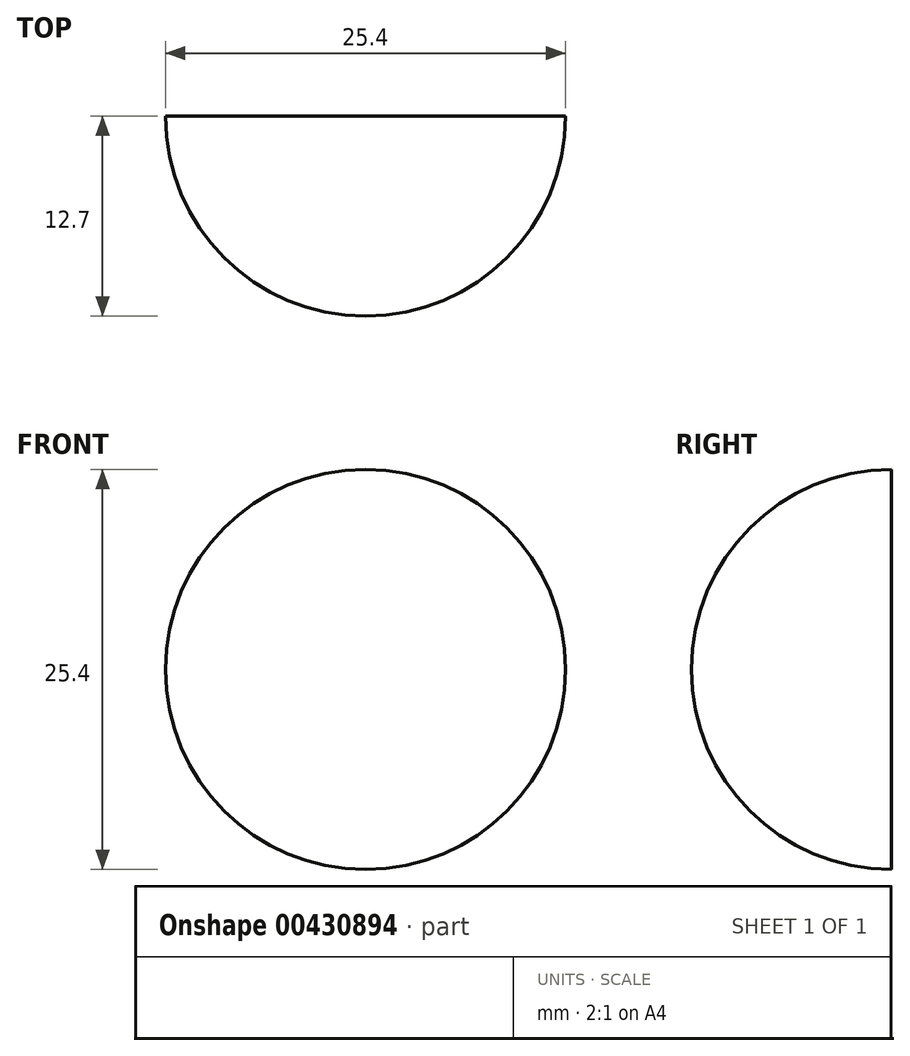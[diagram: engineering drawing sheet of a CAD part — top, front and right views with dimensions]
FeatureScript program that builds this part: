
annotation { "Feature Type Name" : "Feature", "Feature Type Description" : "" }
export const myFeature = defineFeature(function(context is Context, id is Id, definition is map)
    precondition{}
    {
        {
            var Q0;
            Q0=qCreatedBy(makeId("Front.planeOp"),FACE);
            var sketch = newSketch(context, id + "F0", { "sketchPlane" : qUnion([Q0])});
            skArc(sketch, "E0", {"start": v(0, 12.7) * mm, "mid": v(-12.7, 0) * mm, "end": v(0, -12.7) * mm});
            skLineSegment(sketch, "E1", {"start": v(0, 0) * mm, "end": v(0, -12.7) * mm});
            skLineSegment(sketch, "E2", {"start": v(0, 0) * mm, "end": v(0, 12.7) * mm});
            skSolve(sketch);
        }
        {
            var Q0;
            Q0=makeQuery(id+"F0.imprint","IMPRINT",FACE,{"disambiguationData":[TD([[makeQuery(id+"F0.imprint","IMPRINT",EDGE,{"derivedFrom":sQuery(id+"F0.wireOp",EDGE,"E0")}),1.0]])]});
            var Q1;
            Q1=sQuery(id+"F0.wireOp",EDGE,"E2");
            revolve(context, id + "F1", {"entities" : qUnion([Q0]), "axis" : qUnion([Q1]), "revolveType" : RevolveType.FULL});
        }
        {
            var Q0;
            Q0=qCreatedBy(makeId("Front.planeOp"),FACE);
            var sketch = newSketch(context, id + "F2", { "sketchPlane" : qUnion([Q0])});
            skLineSegment(sketch, "E3.bottom", {"start": v(-32.14, 32.14) * mm, "end": v(32.14, 32.14) * mm});
            skLineSegment(sketch, "E3.top", {"start": v(-32.14, -32.14) * mm, "end": v(32.14, -32.14) * mm});
            skLineSegment(sketch, "E3.left", {"start": v(-32.14, 32.14) * mm, "end": v(-32.14, -32.14) * mm});
            skLineSegment(sketch, "E3.right", {"start": v(32.14, 32.14) * mm, "end": v(32.14, -32.14) * mm});
            skLineSegment(sketch, "E4", {"start": v(0, 32.14) * mm, "end": v(0, 0) * mm, "construction": true});
            skLineSegment(sketch, "E5", {"start": v(0, 0) * mm, "end": v(0, -32.14) * mm, "construction": true});
            skLineSegment(sketch, "E6", {"start": v(-32.14, 0) * mm, "end": v(0, 0) * mm});
            skLineSegment(sketch, "E7", {"start": v(0, 0) * mm, "end": v(32.14, 0) * mm, "construction": true});
            skSolve(sketch);
        }
        {
            var Q0;
            Q0=qSketchRegion(id+"F2",true);
            extrude(context, id + "F3", {"entities" : qUnion([Q0]), "operationType" : NewBodyOperationType.REMOVE, "oppositeDirection" : true, "depth" : 12.7 * mm});
        }
        {
            var Q0;
            Q0=makeQuery(id+"F1.opRevolve","SWEPT_BODY",BODY,{"disambiguationData":[OSD([sQuery(id+"F0.wireOp",EDGE,"E0"),sQuery(id+"F0.wireOp",EDGE,"E1"),sQuery(id+"F0.wireOp",EDGE,"E2")])]});
            transform(context, id + "F4", {"entities" : qUnion([Q0]), "transformType" : TransformType.TRANSLATION_3D, "dx" : 0 * mm, "dy" : 0 * mm, "dz" : 0 * mm, "makeCopy" : true});
        }
    });
